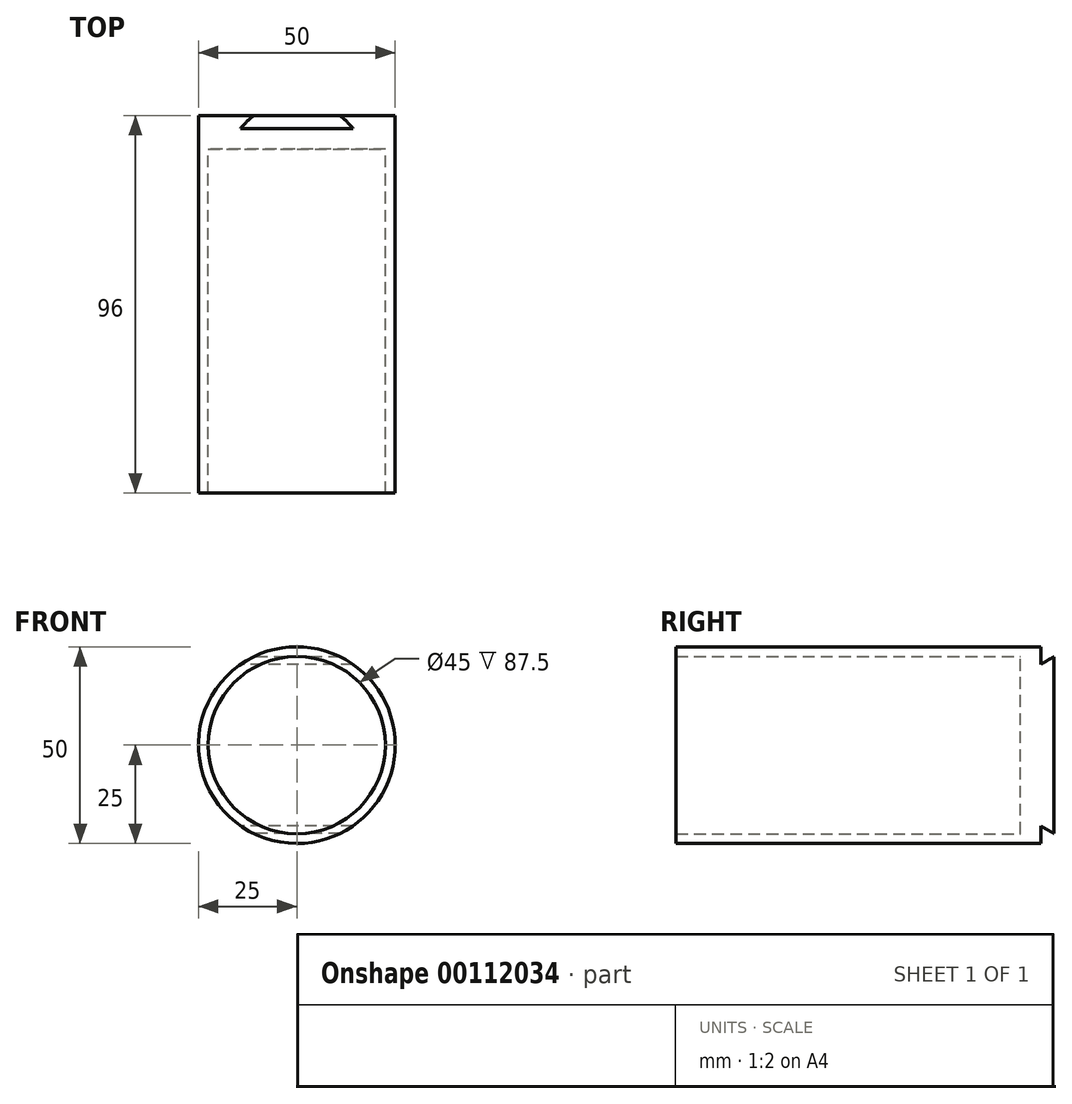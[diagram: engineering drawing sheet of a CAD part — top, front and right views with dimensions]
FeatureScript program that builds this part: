
annotation { "Feature Type Name" : "Feature", "Feature Type Description" : "" }
export const myFeature = defineFeature(function(context is Context, id is Id, definition is map)
    precondition{}
    {
        {
            var Q0;
            Q0=qCreatedBy(makeId("Front.planeOp"),FACE);
            var sketch = newSketch(context, id + "F0", { "sketchPlane" : qUnion([Q0])});
            skCircle(sketch, "E0", {"center": v(0, 0) * mm, "radius": 25 * mm});
            skSolve(sketch);
        }
        {
            var Q0;
            Q0=makeQuery(id+"F0.imprint","IMPRINT",FACE,{"disambiguationData":[TD([[makeQuery(id+"F0.imprint","IMPRINT",EDGE,{"derivedFrom":sQuery(id+"F0.wireOp",EDGE,"E0")}),1.0]])]});
            extrude(context, id + "F1", {"entities" : qUnion([Q0]), "depth" : 90 * mm});
        }
        {
            var Q0;
            Q0=makeQuery(id+"F1.opExtrude","CAP_FACE",FACE,{"disambiguationData":[OSD([sQuery(id+"F0.wireOp",EDGE,"E0")])],"isStart":false});
            var Q1;
            Q1=makeQuery(id+"F1.opExtrude","SWEPT_BODY",BODY,{"disambiguationData":[OSD([sQuery(id+"F0.wireOp",EDGE,"E0")])]});
            shell(context, id + "F2", {"entities" : qUnion([Q0]), "parts" : qUnion([Q1]), "thickness" : 2.5 * mm});
        }
        {
            var Q0;
            Q0=makeQuery(id+"F1.opExtrude","CAP_FACE",FACE,{"disambiguationData":[OSD([sQuery(id+"F0.wireOp",EDGE,"E0")])],"isStart":true});
            extrude(context, id + "F3", {"entities" : qUnion([Q0]), "operationType" : NewBodyOperationType.ADD, "depth" : 6 * mm});
        }
        {
            var Q0;
            Q0=qCreatedBy(makeId("Right.planeOp"),FACE);
            var sketch = newSketch(context, id + "F4", { "sketchPlane" : qUnion([Q0])});
            skLineSegment(sketch, "E1", {"start": v(2.68, 20.53) * mm, "end": v(6, 22.45) * mm});
            skLineSegment(sketch, "E2", {"start": v(6, 22.45) * mm, "end": v(6, -22.45) * mm, "construction": true});
            skLineSegment(sketch, "E3", {"start": v(6, -22.45) * mm, "end": v(2.68, -20.53) * mm});
            skLineSegment(sketch, "E4", {"start": v(2.68, -20.53) * mm, "end": v(2.68, 20.53) * mm, "construction": true});
            skLineSegment(sketch, "E5", {"start": v(2.68, 0) * mm, "end": v(6, 0) * mm, "construction": true});
            skLineSegment(sketch, "E6", {"start": v(2.68, 20.53) * mm, "end": v(2.68, 35.8) * mm});
            skLineSegment(sketch, "E7", {"start": v(2.68, 35.8) * mm, "end": v(6, 35.8) * mm});
            skLineSegment(sketch, "E8", {"start": v(6, 35.8) * mm, "end": v(6, 22.45) * mm});
            skLineSegment(sketch, "E9", {"start": v(2.68, -20.53) * mm, "end": v(2.68, -37.24) * mm});
            skLineSegment(sketch, "E10", {"start": v(2.68, -37.24) * mm, "end": v(6, -37.24) * mm});
            skLineSegment(sketch, "E11", {"start": v(6, -37.24) * mm, "end": v(6, -22.45) * mm});
            skSolve(sketch);
        }
        {
            var Q0;
            Q0=makeQuery(id+"F4.imprint","IMPRINT",FACE,{"disambiguationData":[TD([[makeQuery(id+"F4.imprint","IMPRINT",EDGE,{"derivedFrom":sQuery(id+"F4.wireOp",EDGE,"E1")}),1.0]])]});
            var Q1;
            Q1=makeQuery(id+"F4.imprint","IMPRINT",FACE,{"disambiguationData":[TD([[makeQuery(id+"F4.imprint","IMPRINT",EDGE,{"derivedFrom":sQuery(id+"F4.wireOp",EDGE,"E3")}),1.0]])]});
            extrude(context, id + "F5", {"entities" : qUnion([Q0, Q1]), "operationType" : NewBodyOperationType.REMOVE, "endBound" : BoundingType.SYMMETRIC, "depth" : 100 * mm});
        }
    });
